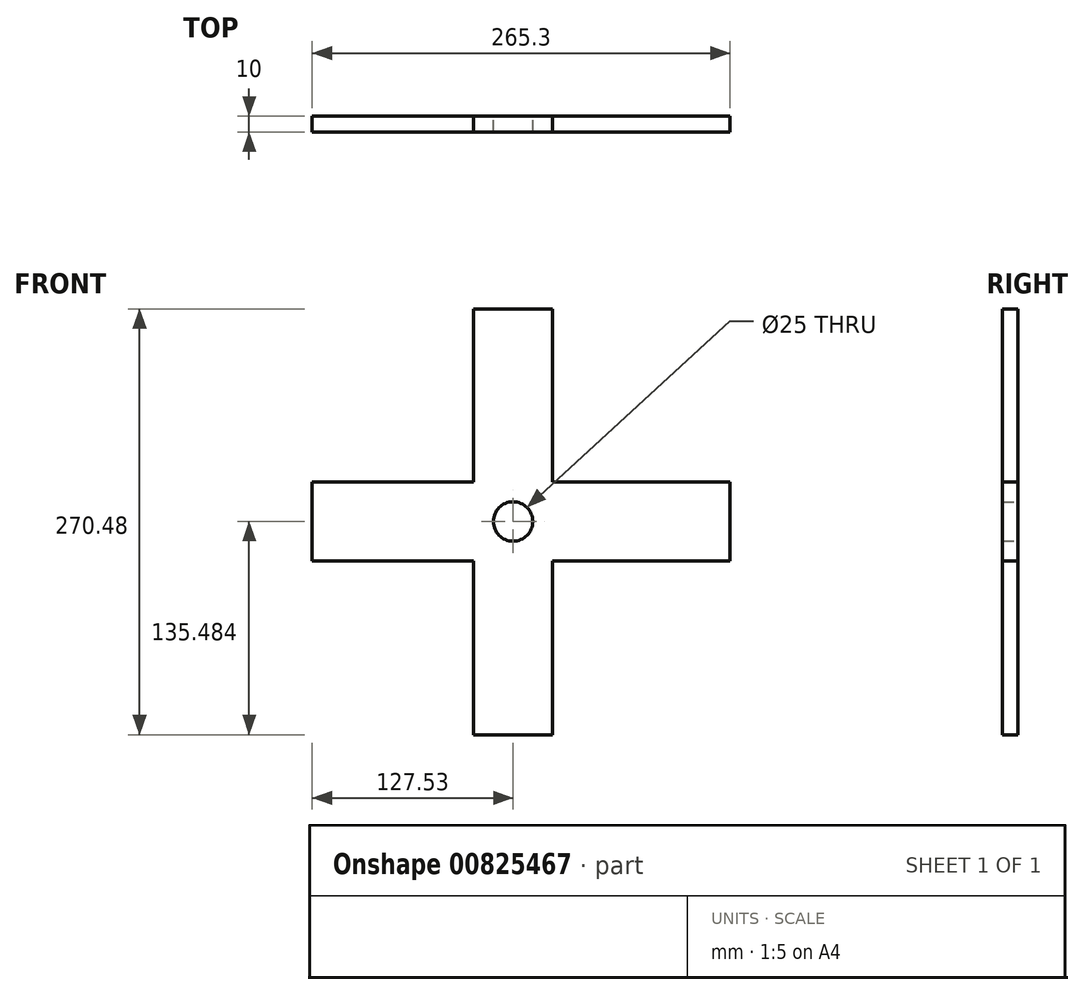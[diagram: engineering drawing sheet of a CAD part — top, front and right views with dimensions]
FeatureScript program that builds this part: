
annotation { "Feature Type Name" : "Feature", "Feature Type Description" : "" }
export const myFeature = defineFeature(function(context is Context, id is Id, definition is map)
    precondition{}
    {
        {
            var Q0;
            Q0=qCreatedBy(makeId("Front.planeOp"),FACE);
            var sketch = newSketch(context, id + "F0", { "sketchPlane" : qUnion([Q0])});
            skLineSegment(sketch, "E0.bottom", {"start": v(-29.74, 131.68) * mm, "end": v(20.26, 131.68) * mm});
            skLineSegment(sketch, "E0.top", {"start": v(-29.74, -138.8) * mm, "end": v(20.26, -138.8) * mm});
            skLineSegment(sketch, "E0.left", {"start": v(-29.74, 131.68) * mm, "end": v(-29.74, 21.68) * mm});
            skLineSegment(sketch, "E0.right", {"start": v(20.26, 131.68) * mm, "end": v(20.26, 21.68) * mm});
            skLineSegment(sketch, "E1.bottom", {"start": v(-132.27, 21.68) * mm, "end": v(-29.74, 21.68) * mm});
            skLineSegment(sketch, "E1.top", {"start": v(-132.27, -28.32) * mm, "end": v(-29.74, -28.32) * mm});
            skLineSegment(sketch, "E1.left", {"start": v(-132.27, 21.68) * mm, "end": v(-132.27, -28.32) * mm});
            skLineSegment(sketch, "E1.right", {"start": v(133.03, 21.68) * mm, "end": v(133.03, -28.32) * mm});
            skArc(sketch, "E2.trimOffspring", {"start": v(-132.2, 21.68) * mm, "mid": v(-132.24, 21.47) * mm, "end": v(-132.27, 21.26) * mm});
            skLineSegment(sketch, "E3.trimOffspring", {"start": v(20.26, -28.32) * mm, "end": v(20.26, -138.8) * mm});
            skLineSegment(sketch, "E4.trimOffspring", {"start": v(20.26, 21.68) * mm, "end": v(133.03, 21.68) * mm});
            skLineSegment(sketch, "E5.trimOffspring", {"start": v(-29.74, -28.32) * mm, "end": v(-29.74, -138.8) * mm});
            skLineSegment(sketch, "E6.trimOffspring", {"start": v(20.26, -28.32) * mm, "end": v(133.03, -28.32) * mm});
            skPoint(sketch, "E7", {"position": v(-4.74, -3.32) * mm});
            skCircle(sketch, "E8", {"center": v(-4.74, -3.32) * mm, "radius": 12.5 * mm});
            skSolve(sketch);
        }
        {
            var Q0;
            Q0 = qSketchRegion(id + "F0", true);
            extrude(context, id + "F1", {"entities" : qUnion([Q0]), "depth" : 10 * mm, "offsetDistance" : 25 * mm});
        }
    });
